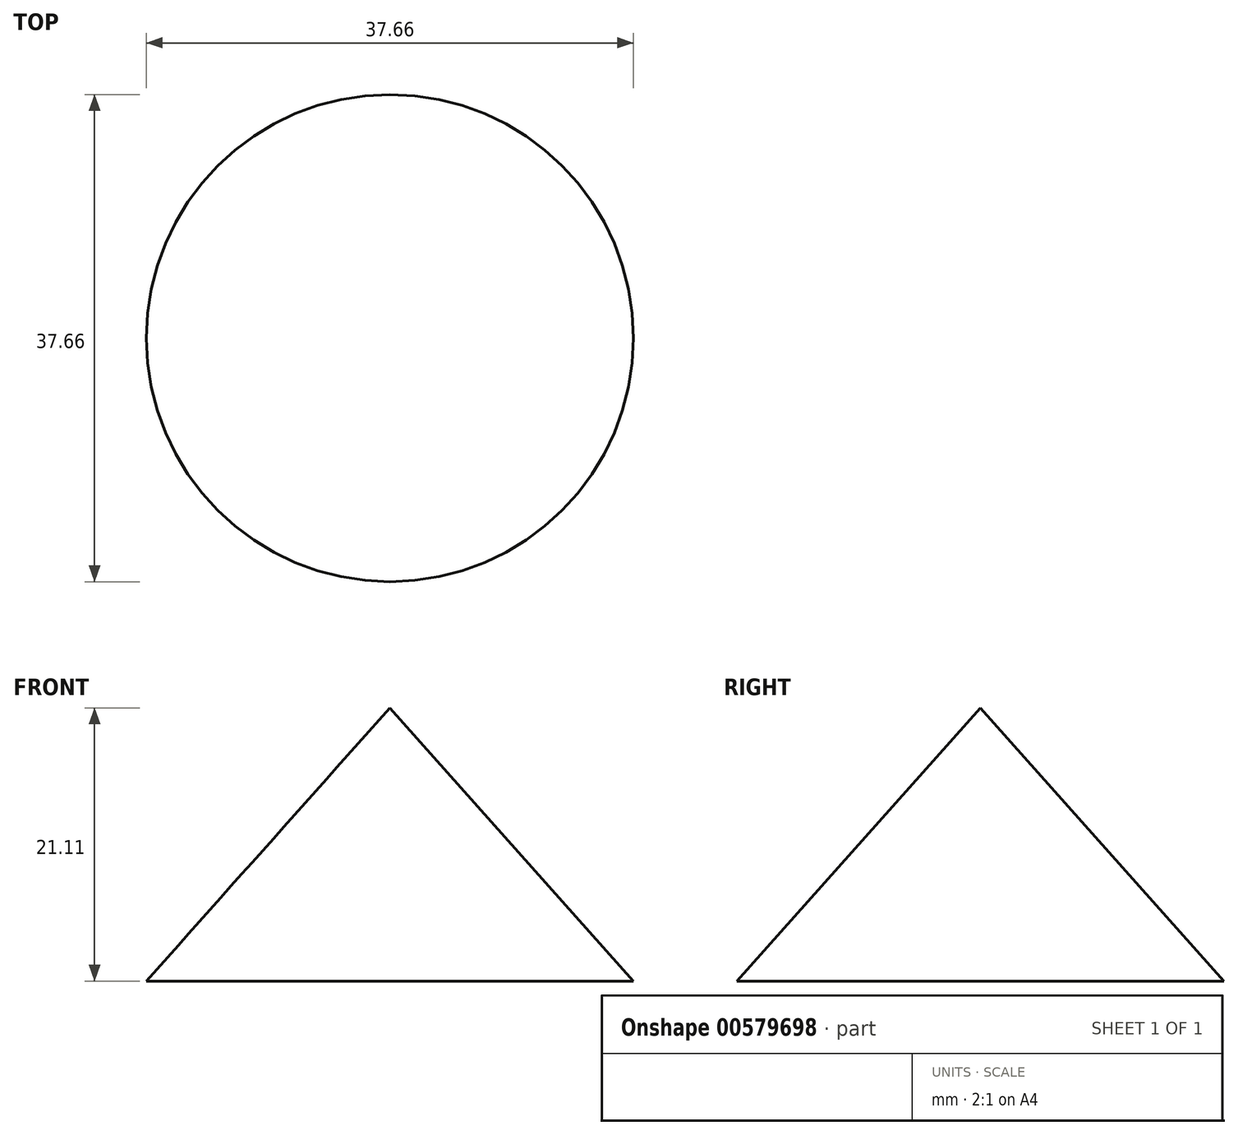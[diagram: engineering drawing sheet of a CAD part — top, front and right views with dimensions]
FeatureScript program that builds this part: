
annotation { "Feature Type Name" : "Feature", "Feature Type Description" : "" }
export const myFeature = defineFeature(function(context is Context, id is Id, definition is map)
    precondition{}
    {
        {
            var Q0;
            Q0=qCreatedBy(makeId("Front.planeOp"),FACE);
            var sketch = newSketch(context, id + "F0", { "sketchPlane" : qUnion([Q0])});
            skLineSegment(sketch, "E0", {"start": v(0, 0) * mm, "end": v(18.83, 0) * mm});
            skLineSegment(sketch, "E1", {"start": v(18.83, 0) * mm, "end": v(0, 21.11) * mm});
            skLineSegment(sketch, "E2", {"start": v(0, 21.11) * mm, "end": v(0, 0) * mm});
            skSolve(sketch);
        }
        {
            var Q0;
            Q0 = qSketchRegion(id + "F0", true);
            var Q1;
            Q1=sQuery(id+"F0.wireOp",EDGE,"E2");
            revolve(context, id + "F1", {"entities" : qUnion([Q0]), "axis" : qUnion([Q1]), "revolveType" : RevolveType.FULL});
        }
    });
